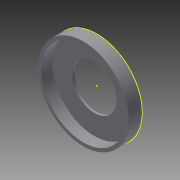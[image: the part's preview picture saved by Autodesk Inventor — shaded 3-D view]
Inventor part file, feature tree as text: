
AUTODESK INVENTOR PART (.ipt)
format: ipt  version: 2013 (Build 170138000, 138)  size: 94,208 bytes
history: native  units: mm
features: sketch x4, extrude x3, other x1
ambient origin geometry x8: Origin, YZ Plane, XZ Plane, XY Plane, X Axis, Y Axis, Z Axis, Center Point
feature tree (8):
  other  "ソリッド1"
  extrude  "押し出し1"  Depth=76.0mm
  extrude  "押し出し2"  Depth=82.0mm
  sketch  "スケッチ3"
  extrude  "押し出し3"  Depth=10.0mm TaperAngle=0.0deg
  sketch  "スケッチ1"
  sketch  "スケッチ2"
  sketch  "スケッチ4"
